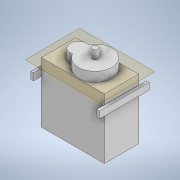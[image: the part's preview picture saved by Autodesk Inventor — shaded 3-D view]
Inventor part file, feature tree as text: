
AUTODESK INVENTOR PART (.ipt)
format: ipt  version: 2021.1 (Build 251245010, 245A)  size: 151,040 bytes
history: native  units: in
note: dims shown in document units (in); Inventor stores cm internally (conversion verified against a paired STEP export)
features: plane x5, extrude x4, sketch x4, mirror x1
ambient origin geometry x8: Origin, YZ Plane, XZ Plane, XY Plane, X Axis, Y Axis, Z Axis, Center Point
bodies: Solid1 (feature_tree)
feature tree (14):
  extrude  "Extrusion1"  Depth=0.4921in
  plane  "Work Plane3"
  plane  "Work Plane4"
  plane  "Work Plane5"
  extrude  "Extrusion2"  Depth=0.8661in
  mirror  "Mirror1"
  plane  "Work Plane6"
  extrude  "Extrusion3"  Depth=0.1102in
  extrude  "Extrusion4"  Depth=0.1102in
  sketch  "Sketch1"  dims[d0=0.9055in d1=0.4921in]
  plane  "Work Plane2"
  sketch  "Sketch2"  dims[d2=0.8661in d3=0.0in d4=0.4528in d5=-0.9055in d6=0.1969in d7=0.2461in]
  sketch  "Sketch3"  dims[d8=0.6299in d9=0.1102in]
  sketch  "Sketch4"  dims[d10=0.0984in d11=0.1102in d12=0.0394in d13=0.0in d14=0.4331in d15=0.4173in d16=0.4803in d17=0.0787in d18=0.1378in d19=0.0in d20=0.1575in d21=0.126in d22=0.0in]
